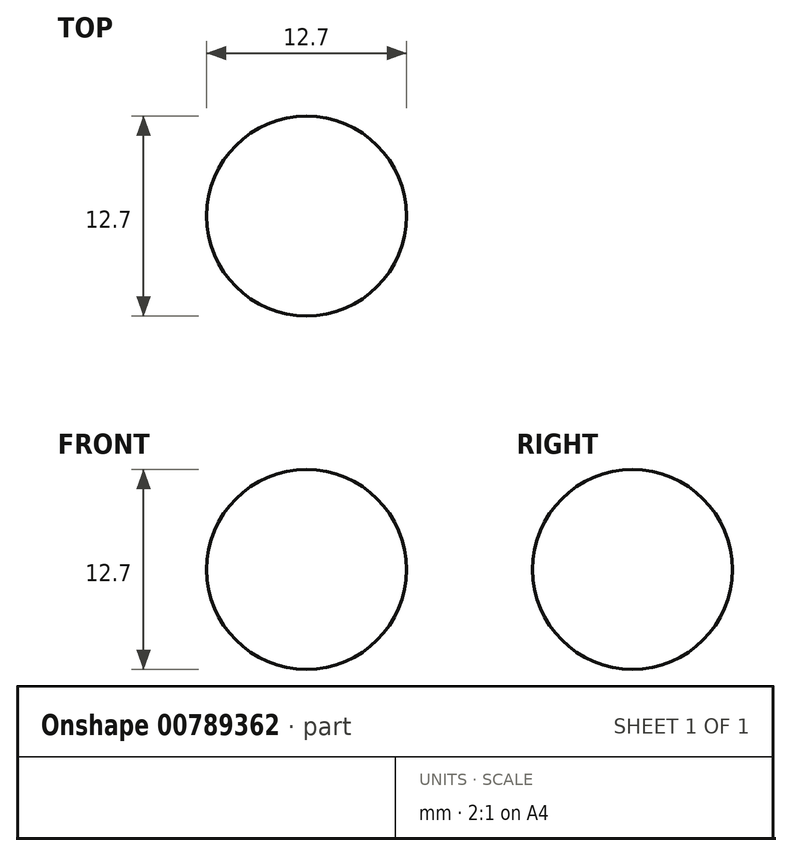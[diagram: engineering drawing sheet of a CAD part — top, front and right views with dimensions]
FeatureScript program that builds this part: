
annotation { "Feature Type Name" : "Feature", "Feature Type Description" : "" }
export const myFeature = defineFeature(function(context is Context, id is Id, definition is map)
    precondition{}
    {
        {
            var Q0;
            Q0=qCreatedBy(makeId("Front.planeOp"),FACE);
            var sketch = newSketch(context, id + "F0", { "sketchPlane" : qUnion([Q0])});
            skLineSegment(sketch, "E0", {"start": v(0, 0) * mm, "end": v(0, 12.7) * mm});
            skArc(sketch, "E1", {"start": v(0, 0) * mm, "mid": v(6.35, 6.35) * mm, "end": v(0, 12.7) * mm});
            skSolve(sketch);
        }
        {
            var Q0;
            Q0=makeQuery(id+"F0.imprint","IMPRINT",FACE,{"disambiguationData":[TD([[makeQuery(id+"F0.imprint","IMPRINT",EDGE,{"derivedFrom":sQuery(id+"F0.wireOp",EDGE,"E0")}),-1.0]])]});
            var Q1;
            Q1=sQuery(id+"F0.wireOp",EDGE,"E0");
            revolve(context, id + "F1", {"entities" : qUnion([Q0]), "axis" : qUnion([Q1]), "revolveType" : RevolveType.FULL});
        }
    });
